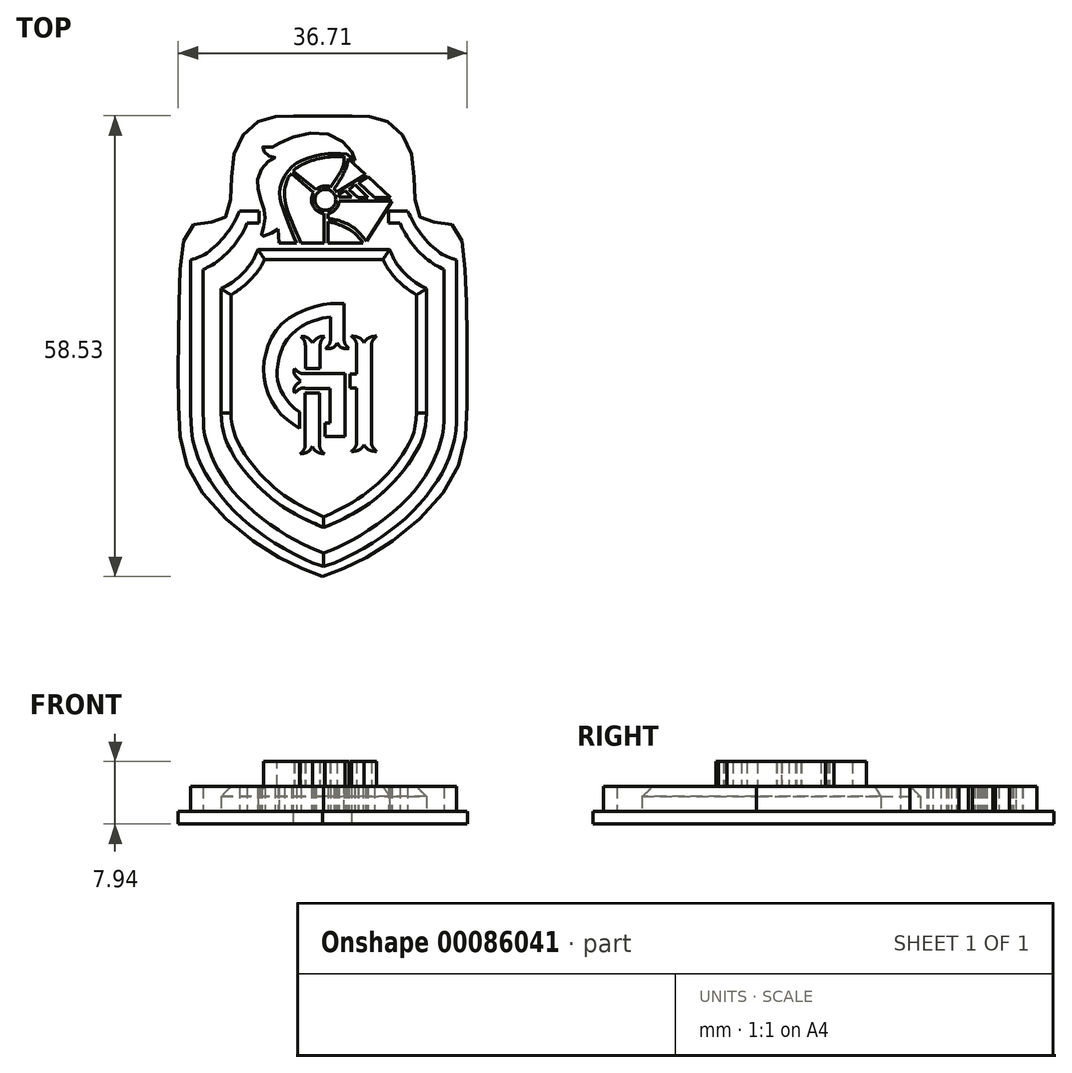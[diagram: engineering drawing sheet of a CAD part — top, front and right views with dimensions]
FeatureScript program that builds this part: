
annotation { "Feature Type Name" : "Feature", "Feature Type Description" : "" }
export const myFeature = defineFeature(function(context is Context, id is Id, definition is map)
    precondition{}
    {
        {
            var Q0;
            Q0=qCreatedBy(makeId("Top.planeOp"),FACE);
            var sketch = newSketch(context, id + "F0", { "sketchPlane" : qUnion([Q0])});
            skLineSegment(sketch, "E0", {"start": v(11.92, -18.8) * mm, "end": v(20.3, -18.8) * mm});
            skLineSegment(sketch, "E1", {"start": v(20.3, -54.14) * mm, "end": v(20.3, -18.8) * mm});
            skFitSpline(sketch, "E2", {"points": [v(11.92, -18.8) * mm, v(10.91, -20.77) * mm, v(7.25, -23.78) * mm], "startDerivative": vector(-2.7, -6.45) * mm, "endDerivative": vector(-8.85, -4.1) * mm});
            skLineSegment(sketch, "E3", {"start": v(7.25, -23.78) * mm, "end": v(7.25, -39.57) * mm});
            skFitSpline(sketch, "E4", {"points": [v(7.25, -39.57) * mm, v(8.2, -43.78) * mm, v(12.1, -49.03) * mm, v(16.4, -52.25) * mm, v(20.3, -54.14) * mm], "startDerivative": vector(0.27, -19.34) * mm, "endDerivative": vector(16.91, -7.51) * mm});
            skLineSegment(sketch, "E5.MirrorCS", {"start": v(28.67, -18.8) * mm, "end": v(20.3, -18.8) * mm});
            skFitSpline(sketch, "E6.MirrorCS", {"points": [v(28.67, -18.8) * mm, v(29.68, -20.77) * mm, v(33.35, -23.78) * mm], "startDerivative": vector(2.7, -6.45) * mm, "endDerivative": vector(8.85, -4.1) * mm});
            skLineSegment(sketch, "E7.MirrorCS", {"start": v(33.35, -23.78) * mm, "end": v(33.35, -39.57) * mm});
            skFitSpline(sketch, "E8.MirrorCS", {"points": [v(33.35, -39.57) * mm, v(32.39, -43.78) * mm, v(28.49, -49.03) * mm, v(24.19, -52.25) * mm, v(20.3, -54.14) * mm], "startDerivative": vector(-0.27, -19.34) * mm, "endDerivative": vector(-16.91, -7.51) * mm});
            skSolve(sketch);
        }
        {
            var Q0;
            Q0=makeQuery(id+"F0.imprint","IMPRINT",FACE,{"disambiguationData":[TD([[makeQuery(id+"F0.imprint","IMPRINT",EDGE,{"derivedFrom":sQuery(id+"F0.wireOp",EDGE,"E0")}),-1.0]])]});
            var Q1;
            Q1=makeQuery(id+"F0.imprint","IMPRINT",FACE,{"disambiguationData":[TD([[makeQuery(id+"F0.imprint","IMPRINT",EDGE,{"derivedFrom":sQuery(id+"F0.wireOp",EDGE,"E1")}),-1.0]])]});
            extrude(context, id + "F1", {"entities" : qUnion([Q0, Q1]), "depth" : 3.17 * mm});
        }
        {
            var Q0;
            Q0=makeQuery(id+"F1.opExtrude","CAP_FACE",FACE,{"disambiguationData":[OSD([sQuery(id+"F0.wireOp",EDGE,"E0"),sQuery(id+"F0.wireOp",EDGE,"E2"),sQuery(id+"F0.wireOp",EDGE,"E3"),sQuery(id+"F0.wireOp",EDGE,"E4"),sQuery(id+"F0.wireOp",EDGE,"E5.MirrorCS"),sQuery(id+"F0.wireOp",EDGE,"E6.MirrorCS"),sQuery(id+"F0.wireOp",EDGE,"E7.MirrorCS"),sQuery(id+"F0.wireOp",EDGE,"E8.MirrorCS")])],"isStart":false});
            var sketch = newSketch(context, id + "F2", { "sketchPlane" : qUnion([Q0])});
            skLineSegment(sketch, "E9", {"start": v(22.87, -30.32) * mm, "end": v(22.87, -25.65) * mm});
            skFitSpline(sketch, "E10", {"points": [v(22.87, -25.65) * mm, v(19.88, -25.86) * mm, v(15.2, -28.05) * mm, v(13.03, -31.62) * mm, v(12.78, -35.48) * mm, v(14.48, -39.27) * mm, v(17.2, -41.52) * mm], "startDerivative": vector(-19.04, 0.4) * mm, "endDerivative": vector(18.48, -12.4) * mm});
            skLineSegment(sketch, "E11", {"start": v(21.15, -30.32) * mm, "end": v(21.15, -27.4) * mm});
            skLineSegment(sketch, "E12", {"start": v(17.2, -41.52) * mm, "end": v(17.2, -39.47) * mm});
            skFitSpline(sketch, "E13", {"points": [v(21.15, -27.4) * mm, v(19.2, -27.78) * mm, v(15.75, -30.07) * mm, v(14.38, -34.12) * mm, v(14.9, -36.8) * mm, v(17.2, -39.47) * mm], "startDerivative": vector(-11.45, -1.22) * mm, "endDerivative": vector(14.53, -10.74) * mm});
            skLineSegment(sketch, "E14", {"start": v(21.07, -40.83) * mm, "end": v(20.48, -40.83) * mm});
            skLineSegment(sketch, "E15", {"start": v(20.48, -40.83) * mm, "end": v(20.48, -42.59) * mm});
            skLineSegment(sketch, "E16", {"start": v(20.48, -42.59) * mm, "end": v(22.97, -42.59) * mm});
            skLineSegment(sketch, "E17", {"start": v(22.97, -42.59) * mm, "end": v(22.97, -34.54) * mm});
            skLineSegment(sketch, "E18", {"start": v(22.97, -34.54) * mm, "end": v(17.99, -34.54) * mm});
            skLineSegment(sketch, "E19", {"start": v(21.07, -40.83) * mm, "end": v(21.07, -36.43) * mm});
            skLineSegment(sketch, "E20", {"start": v(21.07, -36.43) * mm, "end": v(17.99, -36.43) * mm});
            skLineSegment(sketch, "E21", {"start": v(17.93, -43.58) * mm, "end": v(17.93, -37.02) * mm});
            skLineSegment(sketch, "E22", {"start": v(17.93, -37.02) * mm, "end": v(19.75, -37.02) * mm});
            skLineSegment(sketch, "E23", {"start": v(19.75, -37.02) * mm, "end": v(19.75, -43.58) * mm});
            skLineSegment(sketch, "E24", {"start": v(23.66, -36.37) * mm, "end": v(23.66, -34.65) * mm});
            skLineSegment(sketch, "E25", {"start": v(23.66, -34.65) * mm, "end": v(24.49, -34.65) * mm});
            skLineSegment(sketch, "E26", {"start": v(23.66, -36.37) * mm, "end": v(24.49, -36.37) * mm});
            skLineSegment(sketch, "E27", {"start": v(24.49, -36.37) * mm, "end": v(24.49, -43.39) * mm});
            skLineSegment(sketch, "E28", {"start": v(26.34, -30.87) * mm, "end": v(26.34, -43.39) * mm});
            skLineSegment(sketch, "E29", {"start": v(17.95, -30.96) * mm, "end": v(17.95, -33.93) * mm});
            skLineSegment(sketch, "E30", {"start": v(17.95, -33.93) * mm, "end": v(19.83, -33.93) * mm});
            skLineSegment(sketch, "E31", {"start": v(19.83, -33.93) * mm, "end": v(19.83, -30.96) * mm});
            skFitSpline(sketch, "E32", {"points": [v(17.95, -30.96) * mm, v(17.83, -30.4) * mm, v(17.38, -29.83) * mm], "startDerivative": vector(-0.13, 1.2) * mm, "endDerivative": vector(-1, 1.06) * mm});
            skPoint(sketch, "E33.2.internal.snap0", {"position": v(18.9, -33.93) * mm});
            skFitSpline(sketch, "E33", {"points": [v(17.38, -29.83) * mm, v(18.1, -29.94) * mm, v(18.9, -30.65) * mm], "startDerivative": vector(1.62, 0.01) * mm, "endDerivative": vector(1.42, -1.6) * mm});
            skFitSpline(sketch, "E34.MirrorCS", {"points": [v(19.83, -30.96) * mm, v(19.96, -30.4) * mm, v(20.41, -29.83) * mm], "startDerivative": vector(0.13, 1.2) * mm, "endDerivative": vector(1, 1.06) * mm});
            skFitSpline(sketch, "E35.MirrorCS", {"points": [v(20.41, -29.83) * mm, v(19.7, -29.94) * mm, v(18.9, -30.65) * mm], "startDerivative": vector(-1.62, 0.01) * mm, "endDerivative": vector(-1.42, -1.6) * mm});
            skFitSpline(sketch, "E36", {"points": [v(17.99, -34.54) * mm, v(17.39, -34.54) * mm, v(16.57, -33.92) * mm], "startDerivative": vector(-1.37, -0.24) * mm, "endDerivative": vector(-1.45, 1.4) * mm});
            skLineSegment(sketch, "E37", {"start": v(17.99, -35.49) * mm, "end": v(17.67, -35.49) * mm});
            skFitSpline(sketch, "E38", {"points": [v(16.57, -33.92) * mm, v(16.57, -34.62) * mm, v(17.37, -35.49) * mm], "startDerivative": vector(-0.3, -1.63) * mm, "endDerivative": vector(1.82, -1.5) * mm});
            skFitSpline(sketch, "E39.MirrorCS", {"points": [v(17.99, -36.43) * mm, v(17.39, -36.43) * mm, v(16.57, -37.05) * mm], "startDerivative": vector(-1.37, 0.24) * mm, "endDerivative": vector(-1.45, -1.4) * mm});
            skFitSpline(sketch, "E40.MirrorCS", {"points": [v(16.57, -37.05) * mm, v(16.57, -36.35) * mm, v(17.37, -35.49) * mm], "startDerivative": vector(-0.3, 1.63) * mm, "endDerivative": vector(1.82, 1.5) * mm});
            skFitSpline(sketch, "E41", {"points": [v(17.93, -43.58) * mm, v(17.83, -44.12) * mm, v(17.3, -44.75) * mm], "startDerivative": vector(-0.07, -1.21) * mm, "endDerivative": vector(-1.14, -1.13) * mm});
            skFitSpline(sketch, "E42", {"points": [v(17.3, -44.75) * mm, v(18.25, -44.53) * mm, v(18.84, -43.83) * mm], "startDerivative": vector(2.03, 0.19) * mm, "endDerivative": vector(1.03, 1.65) * mm});
            skFitSpline(sketch, "E43.MirrorCS", {"points": [v(19.75, -43.58) * mm, v(19.86, -44.12) * mm, v(20.37, -44.75) * mm], "startDerivative": vector(0.07, -1.21) * mm, "endDerivative": vector(1.14, -1.13) * mm});
            skFitSpline(sketch, "E44.MirrorCS", {"points": [v(20.37, -44.75) * mm, v(19.43, -44.53) * mm, v(18.84, -43.83) * mm], "startDerivative": vector(-2.03, 0.19) * mm, "endDerivative": vector(-1.03, 1.65) * mm});
            skFitSpline(sketch, "E45", {"points": [v(21.15, -30.32) * mm, v(21.03, -30.77) * mm, v(20.52, -31.4) * mm], "startDerivative": vector(-0.15, -1.02) * mm, "endDerivative": vector(-1.06, -1.13) * mm});
            skFitSpline(sketch, "E46", {"points": [v(20.52, -31.4) * mm, v(21.48, -31.26) * mm, v(22.05, -30.61) * mm], "startDerivative": vector(2.04, 0) * mm, "endDerivative": vector(1, 1.59) * mm});
            skFitSpline(sketch, "E47.MirrorCS", {"points": [v(22.87, -30.32) * mm, v(23, -30.77) * mm, v(23.5, -31.4) * mm], "startDerivative": vector(0.15, -1.02) * mm, "endDerivative": vector(1.06, -1.13) * mm});
            skFitSpline(sketch, "E48.MirrorCS", {"points": [v(23.5, -31.4) * mm, v(22.54, -31.26) * mm, v(21.98, -30.61) * mm], "startDerivative": vector(-2.04, 0) * mm, "endDerivative": vector(-1, 1.59) * mm});
            skPoint(sketch, "E49.orphan", {"position": v(24.49, -37.13) * mm});
            skFitSpline(sketch, "E50", {"points": [v(26.34, -30.87) * mm, v(26.48, -30.44) * mm, v(27.02, -29.8) * mm], "startDerivative": vector(0.2, 1) * mm, "endDerivative": vector(1.11, 1.14) * mm});
            skFitSpline(sketch, "E51", {"points": [v(27.02, -29.8) * mm, v(26, -30.02) * mm, v(25.41, -30.62) * mm], "startDerivative": vector(-2.1, -0.2) * mm, "endDerivative": vector(-1.08, -1.47) * mm});
            skFitSpline(sketch, "E52.MirrorCS", {"points": [v(27.02, -44.46) * mm, v(26, -44.24) * mm, v(25.41, -43.64) * mm], "startDerivative": vector(-2.1, 0.2) * mm, "endDerivative": vector(-1.08, 1.47) * mm});
            skFitSpline(sketch, "E53.MirrorCS", {"points": [v(26.34, -43.39) * mm, v(26.48, -43.83) * mm, v(27.02, -44.46) * mm], "startDerivative": vector(0.2, -1) * mm, "endDerivative": vector(1.11, -1.14) * mm});
            skFitSpline(sketch, "E54.MirrorCS", {"points": [v(23.8, -29.8) * mm, v(24.82, -30.02) * mm, v(25.41, -30.62) * mm], "startDerivative": vector(2.1, -0.2) * mm, "endDerivative": vector(1.08, -1.47) * mm});
            skFitSpline(sketch, "E55.MirrorCS", {"points": [v(24.49, -30.87) * mm, v(24.35, -30.44) * mm, v(23.8, -29.8) * mm], "startDerivative": vector(-0.2, 1) * mm, "endDerivative": vector(-1.11, 1.14) * mm});
            skFitSpline(sketch, "E56.MirrorCS", {"points": [v(24.49, -43.39) * mm, v(24.35, -43.83) * mm, v(23.8, -44.46) * mm], "startDerivative": vector(-0.2, -1) * mm, "endDerivative": vector(-1.11, -1.14) * mm});
            skFitSpline(sketch, "E57.MirrorCS", {"points": [v(23.8, -44.46) * mm, v(24.82, -44.24) * mm, v(25.41, -43.64) * mm], "startDerivative": vector(2.1, 0.2) * mm, "endDerivative": vector(1.08, 1.47) * mm});
            skPoint(sketch, "E58.start.orphan", {"position": v(26.34, -37.13) * mm});
            skPoint(sketch, "E59.end.orphan", {"position": v(25.41, -36.32) * mm});
            skPoint(sketch, "E59.start.orphan", {"position": v(25.41, -37.13) * mm});
            skPoint(sketch, "E60.start.orphan", {"position": v(22.01, -30.32) * mm});
            skPoint(sketch, "E61.start.orphan", {"position": v(18.84, -43.58) * mm});
            skPoint(sketch, "E62.end.orphan", {"position": v(24.51, -30.87) * mm});
            skLineSegment(sketch, "E63", {"start": v(24.49, -30.87) * mm, "end": v(24.49, -34.65) * mm});
            skSolve(sketch);
        }
        {
            var Q0;
            Q0 = qSketchRegion(id + "F2", true);
            extrude(context, id + "F3", {"entities" : qUnion([Q0]), "operationType" : NewBodyOperationType.ADD, "depth" : 3.17 * mm});
        }
        {
            var Q0;
            Q0=makeQuery(id+"F1.opExtrude","CAP_EDGE",EDGE,{"disambiguationData":[OSD([sQuery(id+"F0.wireOp",EDGE,"E7.MirrorCS")])],"isStart":false});
            var Q1;
            Q1=makeQuery(id+"F1.opExtrude","CAP_EDGE",EDGE,{"disambiguationData":[OSD([sQuery(id+"F0.wireOp",EDGE,"E8.MirrorCS")])],"isStart":false});
            var Q2;
            Q2=makeQuery(id+"F1.opExtrude","CAP_EDGE",EDGE,{"disambiguationData":[OSD([sQuery(id+"F0.wireOp",EDGE,"E4")])],"isStart":false});
            var Q3;
            Q3=makeQuery(id+"F1.opExtrude","CAP_EDGE",EDGE,{"disambiguationData":[OSD([sQuery(id+"F0.wireOp",EDGE,"E2")])],"isStart":false});
            var Q4;
            Q4=makeQuery(id+"F1.opExtrude","CAP_EDGE",EDGE,{"disambiguationData":[OSD([sQuery(id+"F0.wireOp",EDGE,"E0"),sQuery(id+"F0.wireOp",EDGE,"E5.MirrorCS")])],"isStart":false});
            var Q5;
            Q5=makeQuery(id+"F1.opExtrude","CAP_EDGE",EDGE,{"disambiguationData":[OSD([sQuery(id+"F0.wireOp",EDGE,"E6.MirrorCS")])],"isStart":false});
            chamfer(context, id + "F4", {"entities" : qUnion([Q0, Q1, Q2, Q3, Q4, Q5]), "width" : 1.27 * mm, "tangentPropagation" : true});
        }
        {
            var Q0;
            Q0=qCreatedBy(makeId("Top.planeOp"),FACE);
            var sketch = newSketch(context, id + "F5", { "sketchPlane" : qUnion([Q0])});
            skLineSegment(sketch, "E64", {"start": v(12.05, -13.9) * mm, "end": v(9.61, -13.9) * mm});
            skLineSegment(sketch, "E65", {"start": v(12.05, -13.9) * mm, "end": v(12.05, -15.45) * mm});
            skLineSegment(sketch, "E66", {"start": v(12.05, -15.45) * mm, "end": v(10.55, -15.45) * mm});
            skFitSpline(sketch, "E67", {"points": [v(9.61, -13.9) * mm, v(8.38, -16.19) * mm, v(6.42, -18.46) * mm, v(4.78, -19.63) * mm, v(3.4, -20.14) * mm], "startDerivative": vector(-4.01, -8.44) * mm, "endDerivative": vector(-6.8, -2.06) * mm});
            skLineSegment(sketch, "E68", {"start": v(3.4, -20.14) * mm, "end": v(3.4, -39.62) * mm});
            skFitSpline(sketch, "E69", {"points": [v(3.4, -39.62) * mm, v(3.6, -42.57) * mm, v(4.63, -46.01) * mm, v(6.06, -48.5) * mm, v(8.52, -51.63) * mm, v(11.56, -54.31) * mm, v(15.26, -56.81) * mm, v(19.17, -58.7) * mm, v(20.28, -59.06) * mm], "startDerivative": vector(0.26, -24.27) * mm, "endDerivative": vector(12.69, -3.27) * mm});
            skLineSegment(sketch, "E70", {"start": v(20.28, -59.06) * mm, "end": v(20.28, -57.36) * mm});
            skFitSpline(sketch, "E71", {"points": [v(20.28, -57.36) * mm, v(18, -56.41) * mm, v(14.85, -54.65) * mm, v(11.26, -51.97) * mm, v(8.3, -48.92) * mm, v(6.7, -46.4) * mm, v(5.69, -44.12) * mm, v(5.1, -41.89) * mm, v(4.99, -39.62) * mm], "startDerivative": vector(-19.63, 7.54) * mm, "endDerivative": vector(-0.07, 21.11) * mm});
            skLineSegment(sketch, "E72", {"start": v(4.99, -39.62) * mm, "end": v(4.99, -21.33) * mm});
            skFitSpline(sketch, "E73", {"points": [v(4.99, -21.33) * mm, v(6.62, -20.43) * mm, v(8.9, -18.25) * mm, v(10.37, -15.95) * mm, v(10.55, -15.45) * mm], "startDerivative": vector(6.4, 3.08) * mm, "endDerivative": vector(0.84, 3.13) * mm});
            skSolve(sketch);
        }
        {
            var Q0;
            Q0 = qSketchRegion(id + "F5", true);
            extrude(context, id + "F6", {"entities" : qUnion([Q0]), "depth" : 3.17 * mm});
        }
        {
            var Q0;
            Q0=makeQuery(id+"F6.opExtrude","SWEPT_BODY",BODY,{"disambiguationData":[OSD([sQuery(id+"F5.wireOp",EDGE,"E64"),sQuery(id+"F5.wireOp",EDGE,"E65"),sQuery(id+"F5.wireOp",EDGE,"E66"),sQuery(id+"F5.wireOp",EDGE,"E67"),sQuery(id+"F5.wireOp",EDGE,"E68"),sQuery(id+"F5.wireOp",EDGE,"E69"),sQuery(id+"F5.wireOp",EDGE,"E70"),sQuery(id+"F5.wireOp",EDGE,"E71"),sQuery(id+"F5.wireOp",EDGE,"E72"),sQuery(id+"F5.wireOp",EDGE,"E73")])]});
            var Q1;
            Q1=makeQuery(id+"F6.opExtrude","SWEPT_FACE",FACE,{"disambiguationData":[OSD([sQuery(id+"F5.wireOp",EDGE,"E70")])]});
            mirror(context, id + "F7", {"operationType" : NewBodyOperationType.ADD, "entities" : qUnion([Q0]), "mirrorPlane" : qUnion([Q1])});
        }
        {
            var Q0;
            Q0=qCreatedBy(makeId("Top.planeOp"),FACE);
            var sketch = newSketch(context, id + "F8", { "sketchPlane" : qUnion([Q0])});
            skCircle(sketch, "E74", {"center": v(20.5, -12.49) * mm, "radius": 1.33 * mm});
            skArc(sketch, "E75", {"start": v(19, -11.55) * mm, "mid": v(18.92, -13.28) * mm, "end": v(20.35, -14.24) * mm});
            skLineSegment(sketch, "E76", {"start": v(16.41, -8.8) * mm, "end": v(19.3, -11.2) * mm});
            skLineSegment(sketch, "E77", {"start": v(16.2, -9.17) * mm, "end": v(19, -11.55) * mm});
            skLineSegment(sketch, "E78", {"start": v(20.35, -14.24) * mm, "end": v(20.35, -17.99) * mm});
            skLineSegment(sketch, "E79", {"start": v(20.35, -17.99) * mm, "end": v(17.4, -17.99) * mm});
            skLineSegment(sketch, "E80", {"start": v(20.83, -15.26) * mm, "end": v(20.83, -17.99) * mm});
            skLineSegment(sketch, "E81", {"start": v(20.83, -17.99) * mm, "end": v(25.28, -17.99) * mm});
            skLineSegment(sketch, "E82", {"start": v(25.7, -17.75) * mm, "end": v(28.94, -12.67) * mm});
            skLineSegment(sketch, "E83", {"start": v(28.94, -12.67) * mm, "end": v(22.25, -12.67) * mm});
            skLineSegment(sketch, "E84", {"start": v(25.57, -9.28) * mm, "end": v(21.98, -11.53) * mm});
            skLineSegment(sketch, "E85", {"start": v(25.57, -9.28) * mm, "end": v(23.38, -7.23) * mm});
            skFitSpline(sketch, "E86", {"points": [v(23.38, -7.23) * mm, v(23.23, -8.11) * mm, v(22.44, -9.82) * mm, v(21.6, -11.1) * mm], "startDerivative": vector(-0.24, -3.03) * mm, "endDerivative": vector(-2.41, -3.4) * mm});
            skFitSpline(sketch, "E87", {"points": [v(22.88, -6.95) * mm, v(22.8, -8) * mm, v(22.24, -9.21) * mm, v(21.17, -10.85) * mm], "startDerivative": vector(0.04, -3.67) * mm, "endDerivative": vector(-2.91, -4.33) * mm});
            skFitSpline(sketch, "E88", {"points": [v(16.41, -8.8) * mm, v(17.1, -8.27) * mm, v(19.52, -7.3) * mm, v(22.88, -6.95) * mm], "startDerivative": vector(2.63, 2.4) * mm, "endDerivative": vector(8.14, 0.3) * mm});
            skFitSpline(sketch, "E89", {"points": [v(16.2, -9.17) * mm, v(15.83, -9.63) * mm, v(15.46, -10.57) * mm, v(15.36, -12.6) * mm, v(16.32, -15.42) * mm, v(17.4, -17.99) * mm], "startDerivative": vector(-3.36, -3.57) * mm, "endDerivative": vector(4.13, -9.94) * mm});
            skFitSpline(sketch, "E90", {"points": [v(20.83, -15.26) * mm, v(21.8, -15.5) * mm, v(24, -16.56) * mm, v(25.28, -17.99) * mm], "startDerivative": vector(3.36, -0.61) * mm, "endDerivative": vector(3.05, -4.27) * mm});
            skLineSegment(sketch, "E91", {"start": v(20.82, -14.22) * mm, "end": v(20.82, -14.84) * mm});
            skFitSpline(sketch, "E92", {"points": [v(20.82, -14.84) * mm, v(22.13, -15.11) * mm, v(24.06, -16) * mm, v(25.7, -17.75) * mm], "startDerivative": vector(4.47, -0.73) * mm, "endDerivative": vector(4.06, -5.16) * mm});
            skArc(sketch, "E93.trimOffspring", {"start": v(21.17, -10.85) * mm, "mid": v(20.18, -10.75) * mm, "end": v(19.3, -11.2) * mm});
            skArc(sketch, "E94.trimOffspring", {"start": v(20.82, -14.22) * mm, "mid": v(21.8, -13.68) * mm, "end": v(22.25, -12.67) * mm});
            skFitSpline(sketch, "E95", {"points": [v(24.22, -7.5) * mm, v(23.25, -6.67) * mm], "startDerivative": vector(-0.97, 0.84) * mm, "endDerivative": vector(-0.97, 0.84) * mm});
            skFitSpline(sketch, "E96", {"points": [v(23.25, -6.67) * mm, v(20.4, -6.67) * mm, v(17.4, -7.53) * mm, v(15.63, -9) * mm, v(14.7, -11.3) * mm, v(14.97, -13.18) * mm, v(15.91, -15.79) * mm, v(16.82, -17.96) * mm], "startDerivative": vector(-18.43, 1.16) * mm, "endDerivative": vector(6.47, -15.12) * mm});
            skLineSegment(sketch, "E97", {"start": v(16.82, -17.96) * mm, "end": v(14.6, -17.96) * mm});
            skLineSegment(sketch, "E98", {"start": v(14.6, -17.96) * mm, "end": v(14.47, -16.19) * mm});
            skFitSpline(sketch, "E99", {"points": [v(24.28, -7.5) * mm, v(23.87, -6.4) * mm, v(21.45, -4.35) * mm, v(17.15, -4.3) * mm, v(14.32, -5.51) * mm, v(13.65, -5.82) * mm, v(12.47, -5.8) * mm, v(12.56, -6.08) * mm, v(12.97, -6.66) * mm, v(13.48, -6.97) * mm, v(14.1, -7.1) * mm, v(13.55, -7.38) * mm, v(12.58, -8.32) * mm, v(11.92, -9.88) * mm, v(11.98, -11.18) * mm, v(12.52, -13.11) * mm, v(12.79, -14.08) * mm, v(12.81, -15.23) * mm, v(12.55, -16.37) * mm, v(12.35, -16.98) * mm, v(12.36, -17.16) * mm, v(12.8, -17.05) * mm, v(13.84, -16.66) * mm, v(14.47, -16.19) * mm], "startDerivative": vector(-5.1, 23.14) * mm, "endDerivative": vector(15.49, 13.75) * mm});
            skLineSegment(sketch, "E100", {"start": v(24.72, -10.3) * mm, "end": v(25.92, -9.55) * mm});
            skLineSegment(sketch, "E101", {"start": v(25.92, -9.55) * mm, "end": v(28.8, -12.2) * mm});
            skLineSegment(sketch, "E102", {"start": v(28.8, -12.2) * mm, "end": v(26.75, -12.2) * mm});
            skLineSegment(sketch, "E103", {"start": v(26.75, -12.2) * mm, "end": v(24.72, -10.3) * mm});
            skLineSegment(sketch, "E104", {"start": v(24.3, -10.58) * mm, "end": v(23.48, -11.17) * mm});
            skLineSegment(sketch, "E105", {"start": v(23.48, -11.17) * mm, "end": v(24.66, -12.2) * mm});
            skLineSegment(sketch, "E106", {"start": v(24.66, -12.2) * mm, "end": v(25.94, -12.2) * mm});
            skLineSegment(sketch, "E107", {"start": v(25.94, -12.2) * mm, "end": v(24.3, -10.58) * mm});
            skLineSegment(sketch, "E108", {"start": v(22.16, -11.9) * mm, "end": v(22.98, -11.3) * mm});
            skLineSegment(sketch, "E109", {"start": v(22.98, -11.3) * mm, "end": v(23.84, -12.1) * mm});
            skLineSegment(sketch, "E110", {"start": v(23.84, -12.1) * mm, "end": v(22.22, -12.1) * mm});
            skArc(sketch, "E111.trimOffspring", {"start": v(21.98, -11.53) * mm, "mid": v(21.8, -11.3) * mm, "end": v(21.6, -11.1) * mm});
            skArc(sketch, "E112.trimOffspring", {"start": v(22.22, -12.1) * mm, "mid": v(22.2, -12) * mm, "end": v(22.16, -11.9) * mm});
            skLineSegment(sketch, "E113", {"start": v(24.22, -7.5) * mm, "end": v(24.28, -7.5) * mm});
            skSolve(sketch);
        }
        {
            var Q0;
            Q0 = qSketchRegion(id + "F8", true);
            extrude(context, id + "F9", {"entities" : qUnion([Q0]), "depth" : 3.17 * mm});
        }
        {
            var Q0;
            Q0=qCreatedBy(makeId("Top.planeOp"),FACE);
            var sketch = newSketch(context, id + "F10", { "sketchPlane" : qUnion([Q0])});
            skFitSpline(sketch, "E114", {"points": [v(20.17, -60.35) * mm, v(13.56, -57.32) * mm, v(3.73, -47.93) * mm, v(1.82, -37) * mm, v(2.01, -22.74) * mm, v(3.76, -15.66) * mm, v(7.31, -15.12) * mm, v(8.49, -11.72) * mm, v(9.23, -5.6) * mm, v(12.63, -2.26) * mm, v(16.46, -1.83) * mm], "startDerivative": vector(-59.37, 21.17) * mm, "endDerivative": vector(51.44, -1.01) * mm});
            skLineSegment(sketch, "E115", {"start": v(20.17, -60.35) * mm, "end": v(20.17, -1.83) * mm});
            skLineSegment(sketch, "E116", {"start": v(20.17, -1.83) * mm, "end": v(16.46, -1.83) * mm});
            skFitSpline(sketch, "E117.MirrorCS", {"points": [v(20.17, -60.35) * mm, v(26.78, -57.32) * mm, v(36.6, -47.93) * mm, v(38.52, -37) * mm, v(38.32, -22.74) * mm, v(36.58, -15.66) * mm, v(33.02, -15.12) * mm, v(31.85, -11.72) * mm, v(31.1, -5.6) * mm, v(27.7, -2.26) * mm, v(23.88, -1.83) * mm], "startDerivative": vector(59.37, 21.17) * mm, "endDerivative": vector(-51.44, -1.01) * mm});
            skLineSegment(sketch, "E118.MirrorCS", {"start": v(20.17, -1.83) * mm, "end": v(23.88, -1.83) * mm});
            skSolve(sketch);
        }
        {
            var Q0;
            Q0=makeQuery(id+"F10.imprint","IMPRINT",FACE,{"disambiguationData":[TD([[makeQuery(id+"F10.imprint","IMPRINT",EDGE,{"derivedFrom":sQuery(id+"F10.wireOp",EDGE,"E114")}),-1.0]])]});
            var Q1;
            Q1=makeQuery(id+"F10.imprint","IMPRINT",FACE,{"disambiguationData":[TD([[makeQuery(id+"F10.imprint","IMPRINT",EDGE,{"derivedFrom":sQuery(id+"F10.wireOp",EDGE,"E115")}),-1.0]])]});
            extrude(context, id + "F11", {"entities" : qUnion([Q0, Q1]), "oppositeDirection" : true, "depth" : 1.59 * mm});
        }
    });
